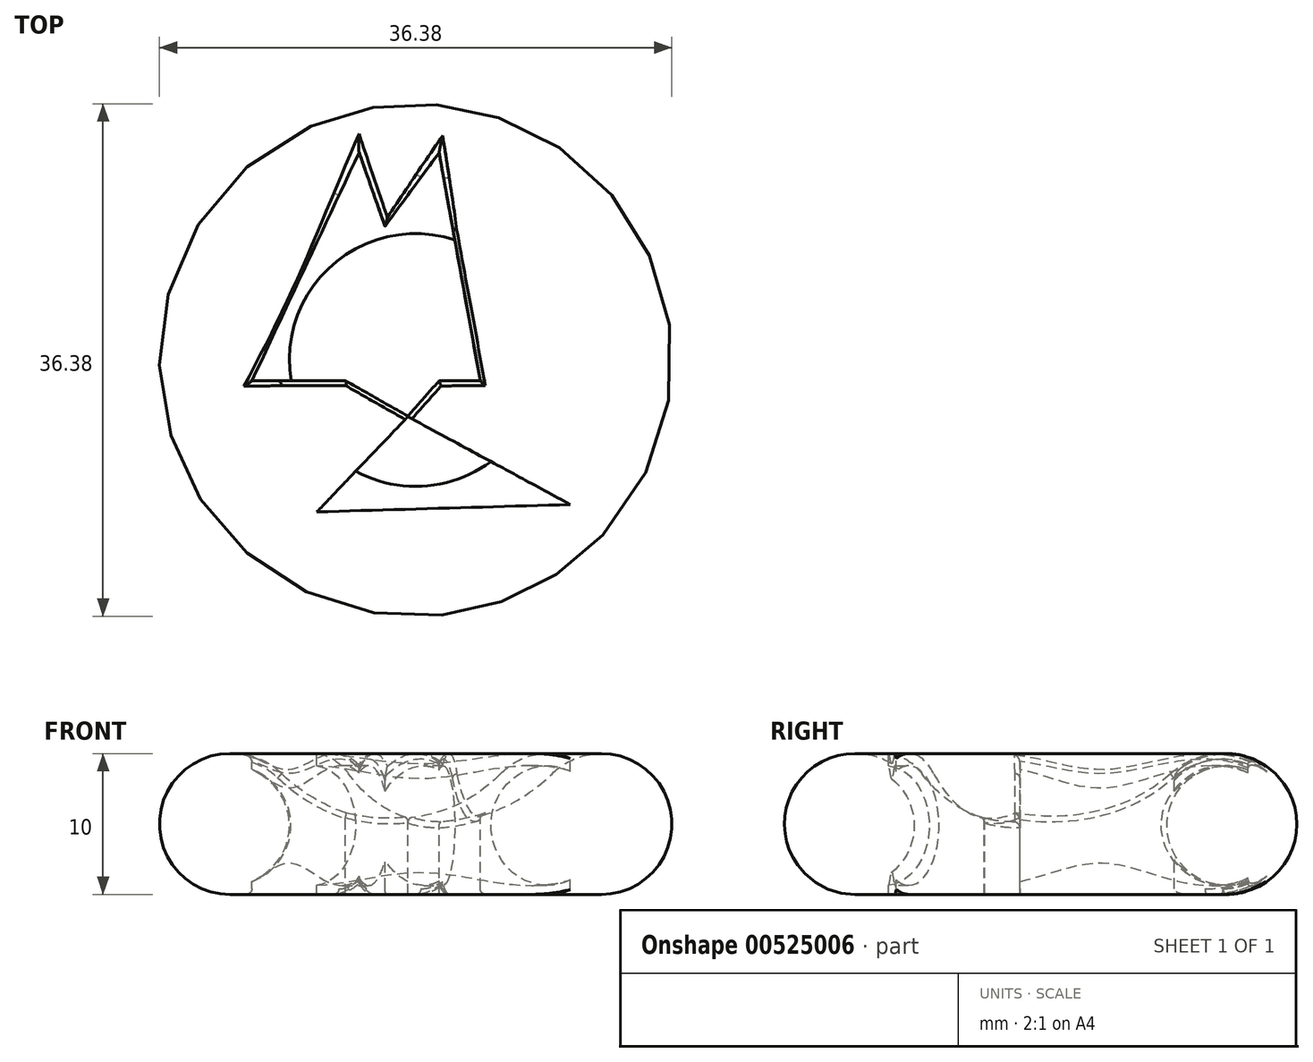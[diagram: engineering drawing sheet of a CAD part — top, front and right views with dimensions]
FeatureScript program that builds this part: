
annotation { "Feature Type Name" : "Feature", "Feature Type Description" : "" }
export const myFeature = defineFeature(function(context is Context, id is Id, definition is map)
    precondition{}
    {
        {
            var Q0;
            Q0=qCreatedBy(makeId("Front.planeOp"),FACE);
            var sketch = newSketch(context, id + "F0", { "sketchPlane" : qUnion([Q0])});
            skArc(sketch, "E0", {"start": v(-9.69, 8.57) * mm, "mid": v(-17.82, 6.9) * mm, "end": v(-13.2, 0) * mm});
            skArc(sketch, "E1", {"start": v(-9.69, 8.57) * mm, "mid": v(-5.23, 5.77) * mm, "end": v(0, 5.1) * mm});
            skLineSegment(sketch, "E2", {"start": v(0, 0) * mm, "end": v(0, 5.1) * mm});
            skPoint(sketch, "E3.orphan", {"position": v(0, 12.2) * mm});
            skLineSegment(sketch, "E4", {"start": v(-13.2, 0) * mm, "end": v(0, 0) * mm});
            skPoint(sketch, "E5", {"position": v(-13.54, 0) * mm});
            skSolve(sketch);
        }
        {
            var Q0;
            Q0=makeQuery(id+"F0.imprint","IMPRINT",FACE,{"disambiguationData":[TD([[makeQuery(id+"F0.imprint","IMPRINT",EDGE,{"derivedFrom":sQuery(id+"F0.wireOp",EDGE,"E0")}),1.0]])]});
            var Q1;
            Q1=sQuery(id+"F0.wireOp",EDGE,"E2");
            revolve(context, id + "F1", {"entities" : qUnion([Q0]), "axis" : qUnion([Q1]), "revolveType" : RevolveType.FULL, "oppositeDirection" : true});
        }
        {
            var Q0;
            Q0=qCreatedBy(makeId("Top.planeOp"),FACE);
            var sketch = newSketch(context, id + "F2", { "sketchPlane" : qUnion([Q0])});
            skLineSegment(sketch, "E6", {"start": v(-4.02, 14.73) * mm, "end": v(-11.63, -1.48) * mm});
            skLineSegment(sketch, "E7", {"start": v(-4.98, -1.48) * mm, "end": v(-11.63, -1.48) * mm});
            skLineSegment(sketch, "E8", {"start": v(-2.18, 9.5) * mm, "end": v(-4.02, 14.73) * mm});
            skLineSegment(sketch, "E9", {"start": v(-2.18, 9.5) * mm, "end": v(1.66, 14.72) * mm});
            skLineSegment(sketch, "E10", {"start": v(1.66, 14.72) * mm, "end": v(4.59, -1.48) * mm});
            skLineSegment(sketch, "E11", {"start": v(4.59, -1.48) * mm, "end": v(1.66, -1.48) * mm});
            skLineSegment(sketch, "E12", {"start": v(1.66, -1.48) * mm, "end": v(-0.55, -3.98) * mm});
            skLineSegment(sketch, "E13", {"start": v(-4.98, -1.48) * mm, "end": v(-0.55, -3.98) * mm});
            skLineSegment(sketch, "E14", {"start": v(-0.55, -4.02) * mm, "end": v(10.98, -10.26) * mm});
            skLineSegment(sketch, "E15", {"start": v(10.98, -10.26) * mm, "end": v(-7.02, -10.78) * mm});
            skLineSegment(sketch, "E16", {"start": v(-7.02, -10.78) * mm, "end": v(-0.55, -4.02) * mm});
            skSolve(sketch);
        }
        {
            var Q0;
            Q0 = qSketchRegion(id + "F2", true);
            extrude(context, id + "F3", {"entities" : qUnion([Q0]), "operationType" : NewBodyOperationType.REMOVE, "endBound" : BoundingType.SYMMETRIC, "oppositeDirection" : true, "depth" : 25 * mm, "offsetDistance" : 25 * mm});
        }
        {
            var Q0;
            Q0=qCreatedBy(makeId("Front.planeOp"),FACE);
            var sketch = newSketch(context, id + "F4", { "sketchPlane" : qUnion([Q0])});
            skCircle(sketch, "E17", {"center": v(-13.22, 4.89) * mm, "radius": 4.25 * mm});
            skSolve(sketch);
        }
        {
            var Q0;
            Q0 = qSketchRegion(id + "F4", true);
            var Q1;
            Q1=sQuery(id+"F0.wireOp",EDGE,"E2");
            revolve(context, id + "F5", {"operationType" : NewBodyOperationType.ADD, "entities" : qUnion([Q0]), "axis" : qUnion([Q1]), "revolveType" : RevolveType.FULL});
        }
        {
            var Q0;
            Q0=makeQuery(id+"F3.boolean.opBoolean","INTERSECT",EDGE,{"disambiguationData":[OD(0.0)],"derivedFrom":[makeQuery(id+"F1.opRevolve","SWEPT_FACE",FACE,{"disambiguationData":[OSD([sQuery(id+"F0.wireOp",EDGE,"E0")])]}),makeQuery(id+"F3.opExtrude","SWEPT_FACE",FACE,{"disambiguationData":[OSD([sQuery(id+"F2.wireOp",EDGE,"E6")])]})]});
            var Q1;
            Q1=makeQuery(id+"F3.boolean.opBoolean","INTERSECT",EDGE,{"disambiguationData":[OD(0.0)],"derivedFrom":[makeQuery(id+"F1.opRevolve","SWEPT_FACE",FACE,{"disambiguationData":[OSD([sQuery(id+"F0.wireOp",EDGE,"E0")])]}),makeQuery(id+"F3.opExtrude","SWEPT_FACE",FACE,{"disambiguationData":[OSD([sQuery(id+"F2.wireOp",EDGE,"E8")])]})]});
            var Q2;
            Q2=makeQuery(id+"F3.boolean.opBoolean","INTERSECT",EDGE,{"derivedFrom":[makeQuery(id+"F1.opRevolve","SWEPT_FACE",FACE,{"disambiguationData":[OSD([sQuery(id+"F0.wireOp",EDGE,"E0")])]}),makeQuery(id+"F3.opExtrude","SWEPT_FACE",FACE,{"disambiguationData":[OSD([sQuery(id+"F2.wireOp",EDGE,"E7")])]})]});
            var Q3;
            Q3=makeQuery(id+"F3.boolean.opBoolean","INTERSECT",EDGE,{"derivedFrom":[makeQuery(id+"F1.opRevolve","SWEPT_FACE",FACE,{"disambiguationData":[OSD([sQuery(id+"F0.wireOp",EDGE,"E1")])]}),makeQuery(id+"F3.opExtrude","SWEPT_FACE",FACE,{"disambiguationData":[OSD([sQuery(id+"F2.wireOp",EDGE,"E7")])]})]});
            var Q4;
            Q4=makeQuery(id+"F3.boolean.opBoolean","INTERSECT",EDGE,{"derivedFrom":[makeQuery(id+"F1.opRevolve","SWEPT_FACE",FACE,{"disambiguationData":[OSD([sQuery(id+"F0.wireOp",EDGE,"E1")])]}),makeQuery(id+"F3.opExtrude","SWEPT_FACE",FACE,{"disambiguationData":[OSD([sQuery(id+"F2.wireOp",EDGE,"E13")])]})]});
            var Q5;
            Q5=makeQuery(id+"F3.boolean.opBoolean","INTERSECT",EDGE,{"disambiguationData":[OD(0.0)],"derivedFrom":[makeQuery(id+"F1.opRevolve","SWEPT_FACE",FACE,{"disambiguationData":[OSD([sQuery(id+"F0.wireOp",EDGE,"E0")])]}),makeQuery(id+"F3.opExtrude","SWEPT_FACE",FACE,{"disambiguationData":[OSD([sQuery(id+"F2.wireOp",EDGE,"E9")])]})]});
            var Q6;
            Q6=makeQuery(id+"F3.boolean.opBoolean","INTERSECT",EDGE,{"disambiguationData":[OD(0.0)],"derivedFrom":[makeQuery(id+"F1.opRevolve","SWEPT_FACE",FACE,{"disambiguationData":[OSD([sQuery(id+"F0.wireOp",EDGE,"E0")])]}),makeQuery(id+"F3.opExtrude","SWEPT_FACE",FACE,{"disambiguationData":[OSD([sQuery(id+"F2.wireOp",EDGE,"E10")])]})]});
            var Q7;
            Q7=makeQuery(id+"F3.boolean.opBoolean","INTERSECT",EDGE,{"derivedFrom":[makeQuery(id+"F1.opRevolve","SWEPT_FACE",FACE,{"disambiguationData":[OSD([sQuery(id+"F0.wireOp",EDGE,"E1")])]}),makeQuery(id+"F3.opExtrude","SWEPT_FACE",FACE,{"disambiguationData":[OSD([sQuery(id+"F2.wireOp",EDGE,"E10")])]})]});
            var Q8;
            Q8=makeQuery(id+"F3.boolean.opBoolean","INTERSECT",EDGE,{"derivedFrom":[makeQuery(id+"F1.opRevolve","SWEPT_FACE",FACE,{"disambiguationData":[OSD([sQuery(id+"F0.wireOp",EDGE,"E1")])]}),makeQuery(id+"F3.opExtrude","SWEPT_FACE",FACE,{"disambiguationData":[OSD([sQuery(id+"F2.wireOp",EDGE,"E11")])]})]});
            var Q9;
            Q9=makeQuery(id+"F3.boolean.opBoolean","INTERSECT",EDGE,{"derivedFrom":[makeQuery(id+"F1.opRevolve","SWEPT_FACE",FACE,{"disambiguationData":[OSD([sQuery(id+"F0.wireOp",EDGE,"E1")])]}),makeQuery(id+"F3.opExtrude","SWEPT_FACE",FACE,{"disambiguationData":[OSD([sQuery(id+"F2.wireOp",EDGE,"E12")])]})]});
            fillet(context, id + "F6", {"entities" : qUnion([Q0, Q1, Q2, Q3, Q4, Q5, Q6, Q7, Q8, Q9]), "radius" : 0.4 * mm, "tangentPropagation" : true, "allowEdgeOverflow" : false});
        }
    });
